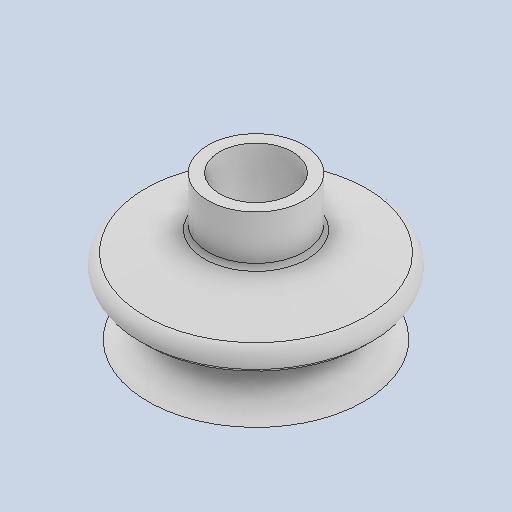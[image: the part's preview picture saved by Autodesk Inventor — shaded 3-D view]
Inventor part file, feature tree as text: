
AUTODESK INVENTOR PART (.ipt)
format: ipt  version: 2024 (Build 280153000, 153)  size: 201,728 bytes
history: native  units: mm
features: other x4, sketch x4
ambient origin geometry x8: Origin, YZ Plane, XZ Plane, XY Plane, X Axis, Y Axis, Z Axis, Center Point
bodies: Body1 (feature_tree)
feature tree (8):
  other  "VENTOSA_B_MIR.ipt"
  other  "Sólido1::VENTOSA_B_MIR.ipt"
  other  "OperaciónIdentificador1"
  sketch  "Boceto1"  dims[d0=10.0mm]
  sketch  "Boceto2"
  sketch  "Boceto3"
  sketch  "Boceto6"
  other  "Sólido1"
